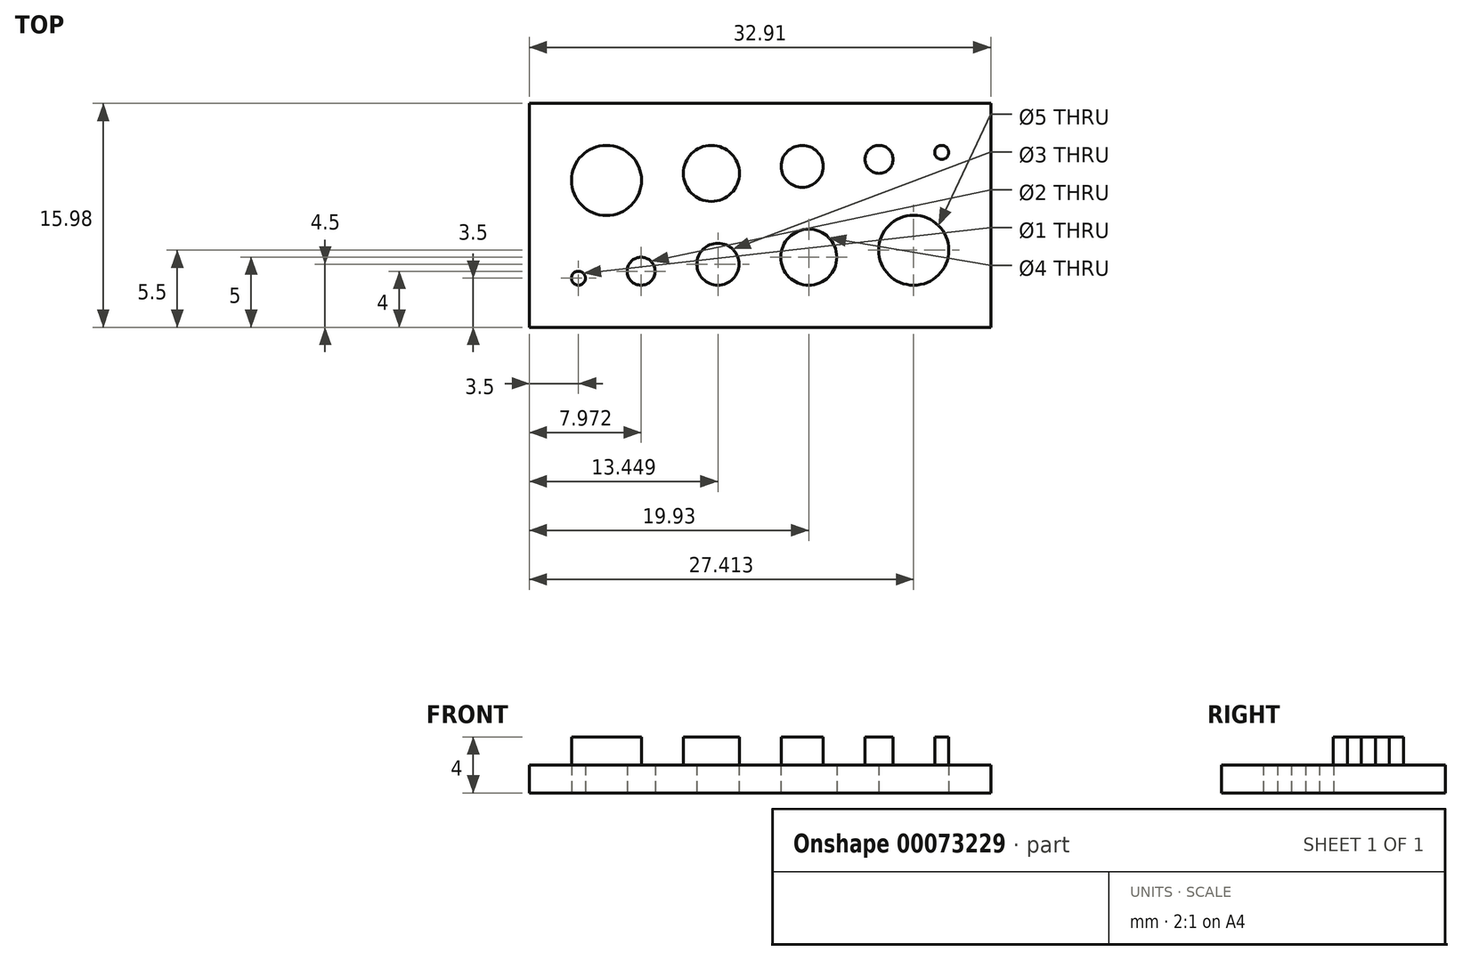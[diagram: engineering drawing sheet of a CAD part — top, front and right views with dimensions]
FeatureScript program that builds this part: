
annotation { "Feature Type Name" : "Feature", "Feature Type Description" : "" }
export const myFeature = defineFeature(function(context is Context, id is Id, definition is map)
    precondition{}
    {
        {
            var Q0;
            Q0=qCreatedBy(makeId("Top.planeOp"),FACE);
            var sketch = newSketch(context, id + "F0", { "sketchPlane" : qUnion([Q0])});
            skLineSegment(sketch, "E0", {"start": v(3, 3) * mm, "end": v(29.91, 3) * mm, "construction": true});
            skCircle(sketch, "E1", {"center": v(3.5, 3.5) * mm, "radius": 0.5 * mm});
            skPoint(sketch, "E1.first.point", {"position": v(3.5, 3) * mm});
            skCircle(sketch, "E2", {"center": v(7.97, 4) * mm, "radius": 1 * mm});
            skPoint(sketch, "E2.first.point", {"position": v(7.97, 3) * mm});
            skCircle(sketch, "E3", {"center": v(13.45, 4.5) * mm, "radius": 1.5 * mm});
            skPoint(sketch, "E3.first.point", {"position": v(13.45, 3) * mm});
            skCircle(sketch, "E4", {"center": v(27.41, 5.5) * mm, "radius": 2.5 * mm});
            skPoint(sketch, "E4.first.point", {"position": v(27.41, 3) * mm});
            skCircle(sketch, "E5", {"center": v(19.93, 5) * mm, "radius": 2 * mm});
            skPoint(sketch, "E5.first.point", {"position": v(19.93, 3) * mm});
            skPoint(sketch, "E6", {"position": v(29.91, 5.5) * mm});
            skPoint(sketch, "E7", {"position": v(3, 3.5) * mm});
            skPoint(sketch, "E8", {"position": v(16.46, 3) * mm});
            skLineSegment(sketch, "E9", {"start": v(16.46, -2.82) * mm, "end": v(16.46, 21.57) * mm, "construction": true});
            skLineSegment(sketch, "E10", {"start": v(0.18, 7.5) * mm, "end": v(35.66, 7.5) * mm, "construction": true});
            skCircle(sketch, "E11.MirrorC", {"center": v(29.41, 12.48) * mm, "radius": 0.5 * mm});
            skCircle(sketch, "E12.MirrorC", {"center": v(24.94, 11.98) * mm, "radius": 1 * mm});
            skCircle(sketch, "E13.MirrorC", {"center": v(19.46, 11.48) * mm, "radius": 1.5 * mm});
            skCircle(sketch, "E14.MirrorC", {"center": v(12.98, 10.98) * mm, "radius": 2 * mm});
            skCircle(sketch, "E15.MirrorC", {"center": v(5.5, 10.48) * mm, "radius": 2.5 * mm});
            skLineSegment(sketch, "E16.bottom", {"start": v(0, 0) * mm, "end": v(32.91, 0) * mm});
            skLineSegment(sketch, "E16.top", {"start": v(0, 15.98) * mm, "end": v(32.91, 15.98) * mm});
            skLineSegment(sketch, "E16.left", {"start": v(0, 0) * mm, "end": v(0, 15.98) * mm});
            skLineSegment(sketch, "E16.right", {"start": v(32.91, 0) * mm, "end": v(32.91, 15.98) * mm});
            skLineSegment(sketch, "E17", {"start": v(2.14, 12.98) * mm, "end": v(29.91, 12.98) * mm, "construction": true});
            skPoint(sketch, "E18", {"position": v(3, 10.48) * mm});
            skPoint(sketch, "E19", {"position": v(29.91, 12.48) * mm});
            skSolve(sketch);
        }
        {
            var Q0;
            Q0 = qSketchRegion(id + "F0", true);
            var Q1;
            Q1=makeQuery(id+"F0.imprint","IMPRINT",FACE,{"disambiguationData":[TD([[makeQuery(id+"F0.imprint","IMPRINT",EDGE,{"derivedFrom":sQuery(id+"F0.wireOp",EDGE,"E15.MirrorC")}),1.0]])]});
            var Q2;
            Q2=makeQuery(id+"F0.imprint","IMPRINT",FACE,{"disambiguationData":[TD([[makeQuery(id+"F0.imprint","IMPRINT",EDGE,{"derivedFrom":sQuery(id+"F0.wireOp",EDGE,"E14.MirrorC")}),1.0]])]});
            var Q3;
            Q3=makeQuery(id+"F0.imprint","IMPRINT",FACE,{"disambiguationData":[TD([[makeQuery(id+"F0.imprint","IMPRINT",EDGE,{"derivedFrom":sQuery(id+"F0.wireOp",EDGE,"E13.MirrorC")}),1.0]])]});
            var Q4;
            Q4=makeQuery(id+"F0.imprint","IMPRINT",FACE,{"disambiguationData":[TD([[makeQuery(id+"F0.imprint","IMPRINT",EDGE,{"derivedFrom":sQuery(id+"F0.wireOp",EDGE,"E12.MirrorC")}),1.0]])]});
            var Q5;
            Q5=makeQuery(id+"F0.imprint","IMPRINT",FACE,{"disambiguationData":[TD([[makeQuery(id+"F0.imprint","IMPRINT",EDGE,{"derivedFrom":sQuery(id+"F0.wireOp",EDGE,"E11.MirrorC")}),1.0]])]});
            extrude(context, id + "F1", {"entities" : qUnion([Q0, Q1, Q2, Q3, Q4, Q5]), "depth" : 2 * mm});
        }
        {
            var Q0;
            Q0=makeQuery(id+"F1.opExtrude","CAP_FACE",FACE,{"disambiguationData":[OSD([sQuery(id+"F0.wireOp",EDGE,"E1"),sQuery(id+"F0.wireOp",EDGE,"E2"),sQuery(id+"F0.wireOp",EDGE,"E3"),sQuery(id+"F0.wireOp",EDGE,"E4"),sQuery(id+"F0.wireOp",EDGE,"E5"),sQuery(id+"F0.wireOp",EDGE,"E16.bottom"),sQuery(id+"F0.wireOp",EDGE,"E16.top"),sQuery(id+"F0.wireOp",EDGE,"E16.left"),sQuery(id+"F0.wireOp",EDGE,"E16.right")])],"isStart":false});
            var sketch = newSketch(context, id + "F2", { "sketchPlane" : qUnion([Q0])});
            skCircle(sketch, "E20.16", {"center": v(29.41, 12.48) * mm, "radius": 0.5 * mm});
            skCircle(sketch, "E20.17", {"center": v(24.94, 11.98) * mm, "radius": 1 * mm});
            skCircle(sketch, "E20.18", {"center": v(19.46, 11.48) * mm, "radius": 1.5 * mm});
            skCircle(sketch, "E20.19", {"center": v(12.98, 10.98) * mm, "radius": 2 * mm});
            skCircle(sketch, "E20.20", {"center": v(5.5, 10.48) * mm, "radius": 2.5 * mm});
            skPoint(sketch, "E20.26", {"position": v(3, 10.48) * mm});
            skPoint(sketch, "E20.27", {"position": v(29.91, 12.48) * mm});
            skSolve(sketch);
        }
        {
            var Q0;
            Q0 = qSketchRegion(id + "F2", true);
            extrude(context, id + "F3", {"entities" : qUnion([Q0]), "operationType" : NewBodyOperationType.ADD, "depth" : 2 * mm});
        }
    });
